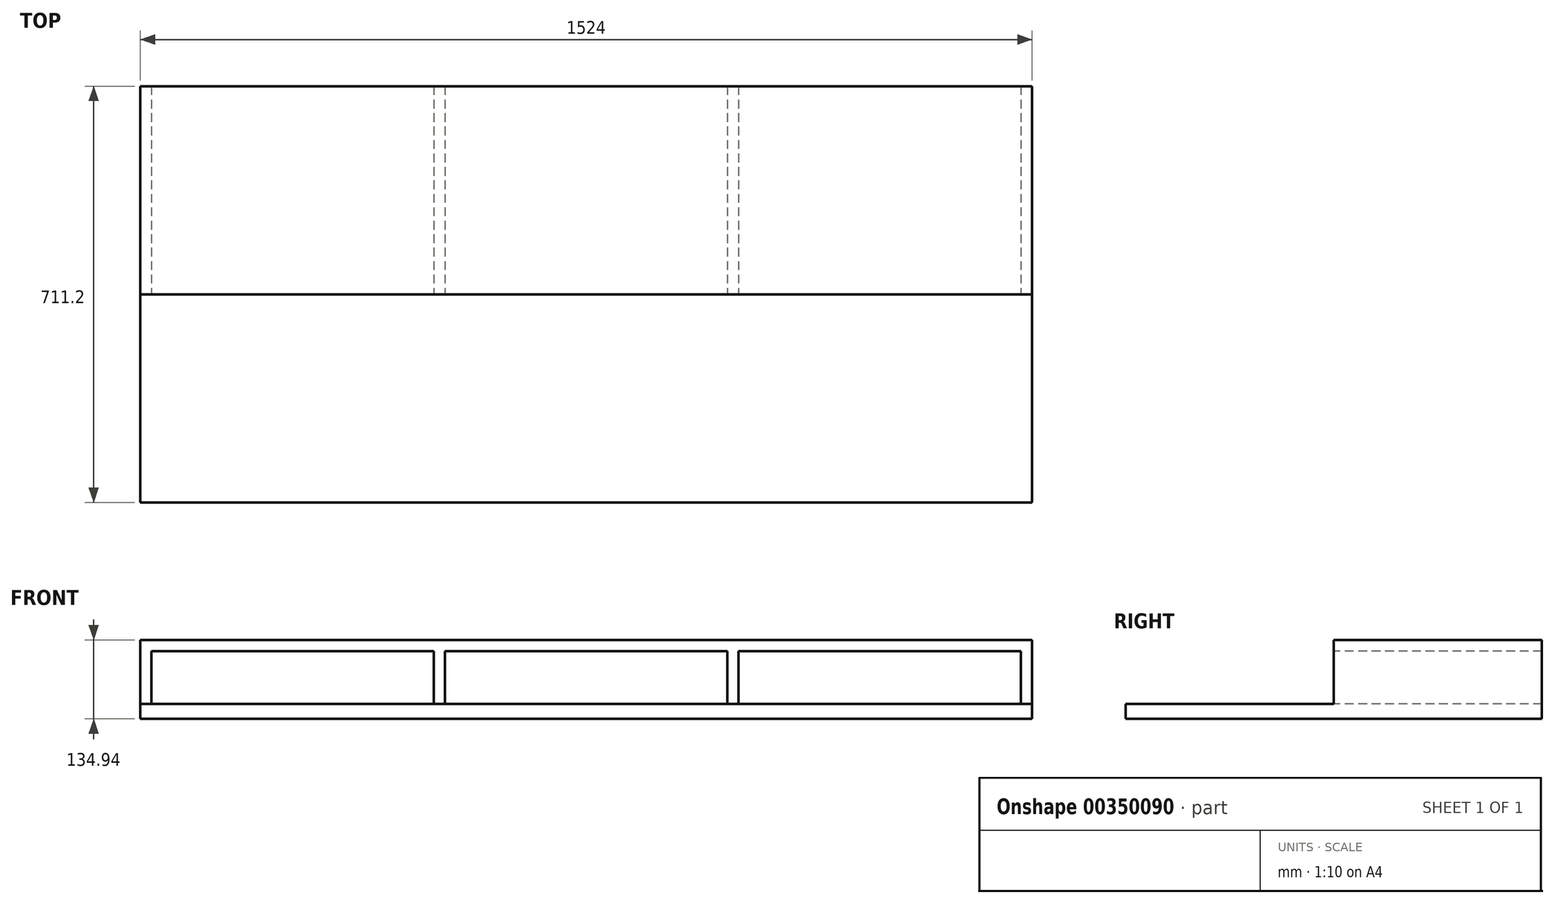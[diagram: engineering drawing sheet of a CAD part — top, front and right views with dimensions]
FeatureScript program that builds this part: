
annotation { "Feature Type Name" : "Feature", "Feature Type Description" : "" }
export const myFeature = defineFeature(function(context is Context, id is Id, definition is map)
    precondition{}
    {
        {
            var Q0;
            Q0=qCreatedBy(makeId("Top.planeOp"),FACE);
            var sketch = newSketch(context, id + "F0", { "sketchPlane" : qUnion([Q0])});
            skLineSegment(sketch, "E0.bottom", {"start": v(0, 0) * mm, "end": v(1524, 0) * mm});
            skLineSegment(sketch, "E0.top", {"start": v(0, 711.2) * mm, "end": v(1524, 711.2) * mm});
            skLineSegment(sketch, "E0.left", {"start": v(0, 0) * mm, "end": v(0, 711.2) * mm});
            skLineSegment(sketch, "E0.right", {"start": v(1524, 0) * mm, "end": v(1524, 711.2) * mm});
            skSolve(sketch);
        }
        {
            var Q0;
            Q0=makeQuery(id+"F0.imprint","IMPRINT",FACE,{"disambiguationData":[TD([[makeQuery(id+"F0.imprint","IMPRINT",EDGE,{"derivedFrom":sQuery(id+"F0.wireOp",EDGE,"E0.bottom")}),1.0]])]});
            extrude(context, id + "F1", {"entities" : qUnion([Q0]), "depth" : 25.4 * mm});
        }
        {
            var Q0;
            Q0=makeQuery(id+"F1.opExtrude","CAP_FACE",FACE,{"disambiguationData":[OSD([sQuery(id+"F0.wireOp",EDGE,"E0.bottom"),sQuery(id+"F0.wireOp",EDGE,"E0.top"),sQuery(id+"F0.wireOp",EDGE,"E0.left"),sQuery(id+"F0.wireOp",EDGE,"E0.right")])],"isStart":false});
            var sketch = newSketch(context, id + "F2", { "sketchPlane" : qUnion([Q0])});
            skLineSegment(sketch, "E1.bottom", {"start": v(0, 711.2) * mm, "end": v(19.05, 711.2) * mm});
            skLineSegment(sketch, "E1.top", {"start": v(0, 355.6) * mm, "end": v(19.05, 355.6) * mm});
            skLineSegment(sketch, "E1.left", {"start": v(0, 711.2) * mm, "end": v(0, 355.6) * mm});
            skLineSegment(sketch, "E1.right", {"start": v(19.05, 711.2) * mm, "end": v(19.05, 355.6) * mm});
            skLineSegment(sketch, "E2.bottom", {"start": v(501.65, 711.2) * mm, "end": v(520.7, 711.2) * mm});
            skLineSegment(sketch, "E2.top", {"start": v(501.65, 355.6) * mm, "end": v(520.7, 355.6) * mm});
            skLineSegment(sketch, "E2.left", {"start": v(501.65, 711.2) * mm, "end": v(501.65, 355.6) * mm});
            skLineSegment(sketch, "E2.right", {"start": v(520.7, 711.2) * mm, "end": v(520.7, 355.6) * mm});
            skLineSegment(sketch, "E3", {"start": v(762, 711.2) * mm, "end": v(762, 0) * mm, "construction": true});
            skLineSegment(sketch, "E4.MirrorCS", {"start": v(1022.35, 355.6) * mm, "end": v(1003.3, 355.6) * mm});
            skLineSegment(sketch, "E5.MirrorCS", {"start": v(1022.35, 711.2) * mm, "end": v(1003.3, 711.2) * mm});
            skLineSegment(sketch, "E6.MirrorCS", {"start": v(1524, 355.6) * mm, "end": v(1504.95, 355.6) * mm});
            skLineSegment(sketch, "E7.MirrorCS", {"start": v(1524, 711.2) * mm, "end": v(1504.95, 711.2) * mm});
            skLineSegment(sketch, "E8.MirrorCS", {"start": v(1022.35, 711.2) * mm, "end": v(1022.35, 355.6) * mm});
            skLineSegment(sketch, "E9.MirrorCS", {"start": v(1504.95, 711.2) * mm, "end": v(1504.95, 355.6) * mm});
            skLineSegment(sketch, "E10.MirrorCS", {"start": v(1524, 711.2) * mm, "end": v(1524, 355.6) * mm});
            skLineSegment(sketch, "E11.MirrorCS", {"start": v(1003.3, 711.2) * mm, "end": v(1003.3, 355.6) * mm});
            skSolve(sketch);
        }
        {
            var Q0;
            Q0=makeQuery(id+"F2.imprint","IMPRINT",FACE,{"disambiguationData":[TD([[makeQuery(id+"F2.imprint","IMPRINT",EDGE,{"derivedFrom":sQuery(id+"F2.wireOp",EDGE,"E1.bottom")}),-1.0]])]});
            var Q1;
            Q1=makeQuery(id+"F2.imprint","IMPRINT",FACE,{"disambiguationData":[TD([[makeQuery(id+"F2.imprint","IMPRINT",EDGE,{"derivedFrom":sQuery(id+"F2.wireOp",EDGE,"E2.bottom")}),-1.0]])]});
            var Q2;
            Q2=makeQuery(id+"F2.imprint","IMPRINT",FACE,{"disambiguationData":[TD([[makeQuery(id+"F2.imprint","IMPRINT",EDGE,{"derivedFrom":sQuery(id+"F2.wireOp",EDGE,"E4.MirrorCS")}),-1.0]])]});
            var Q3;
            Q3=makeQuery(id+"F2.imprint","IMPRINT",FACE,{"disambiguationData":[TD([[makeQuery(id+"F2.imprint","IMPRINT",EDGE,{"derivedFrom":sQuery(id+"F2.wireOp",EDGE,"E6.MirrorCS")}),-1.0]])]});
            extrude(context, id + "F3", {"entities" : qUnion([Q0, Q1, Q2, Q3]), "operationType" : NewBodyOperationType.ADD, "depth" : 90.49 * mm});
        }
        {
            var Q0;
            Q0=makeQuery(id+"F3.opExtrude","CAP_FACE",FACE,{"disambiguationData":[OSD([sQuery(id+"F2.wireOp",EDGE,"E1.bottom"),sQuery(id+"F2.wireOp",EDGE,"E1.top"),sQuery(id+"F2.wireOp",EDGE,"E1.left"),sQuery(id+"F2.wireOp",EDGE,"E1.right")])],"isStart":false});
            var sketch = newSketch(context, id + "F4", { "sketchPlane" : qUnion([Q0])});
            skLineSegment(sketch, "E12.bottom", {"start": v(0, 711.2) * mm, "end": v(1524, 711.2) * mm});
            skLineSegment(sketch, "E12.top", {"start": v(0, 355.6) * mm, "end": v(1524, 355.6) * mm});
            skLineSegment(sketch, "E12.left", {"start": v(0, 711.2) * mm, "end": v(0, 355.6) * mm});
            skLineSegment(sketch, "E12.right", {"start": v(1524, 711.2) * mm, "end": v(1524, 355.6) * mm});
            skSolve(sketch);
        }
        {
            var Q0;
            Q0=qSketchRegion(id+"F4",true);
            extrude(context, id + "F5", {"entities" : qUnion([Q0]), "operationType" : NewBodyOperationType.ADD, "depth" : 19.05 * mm});
        }
    });
